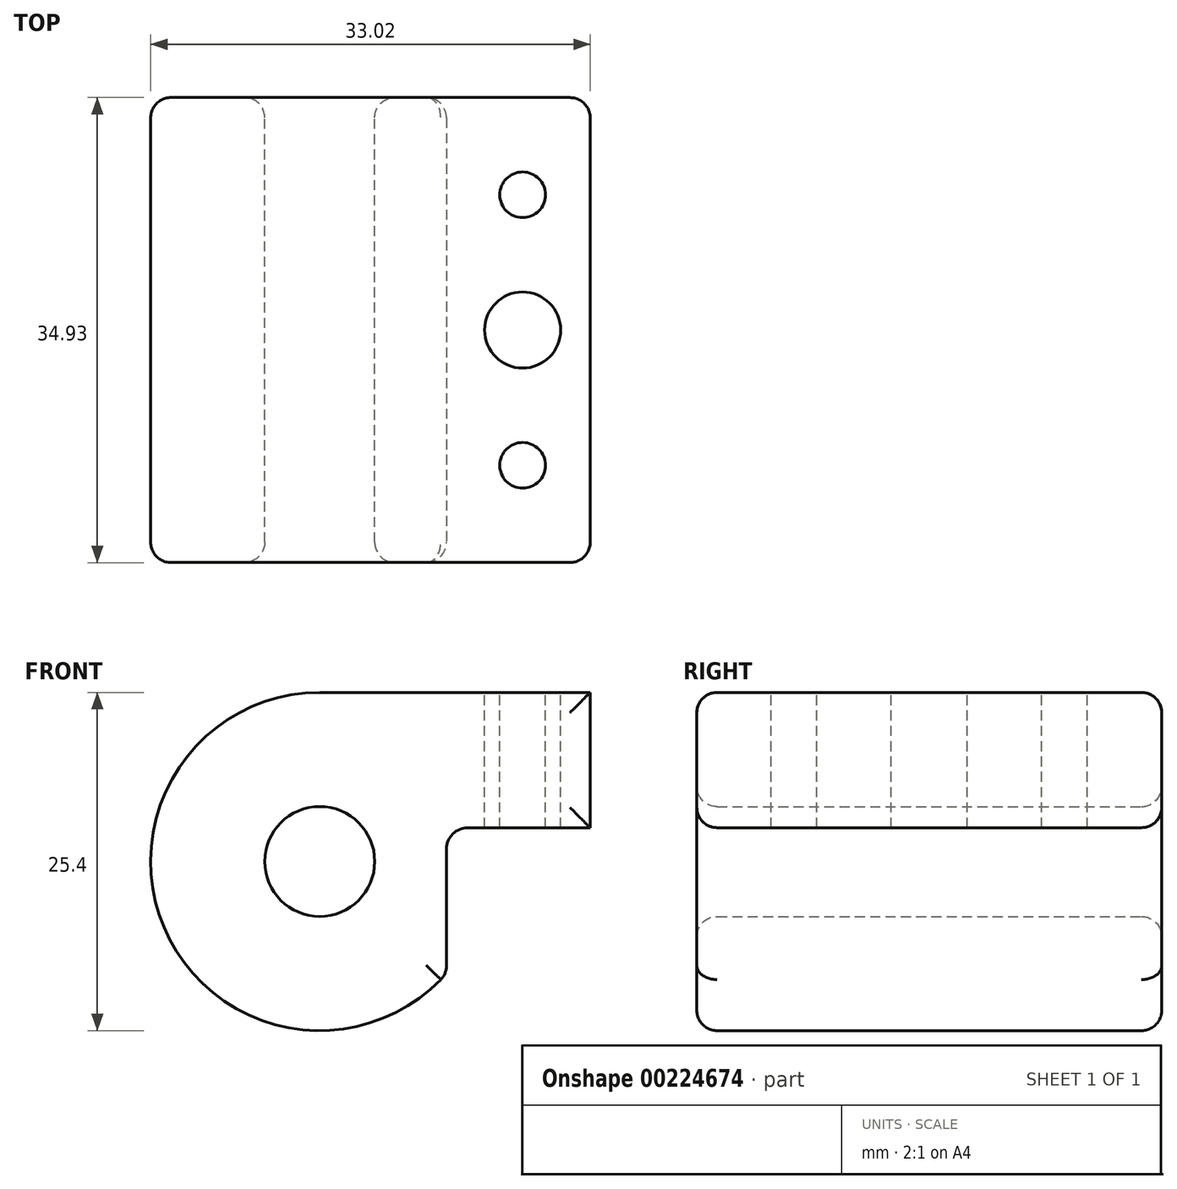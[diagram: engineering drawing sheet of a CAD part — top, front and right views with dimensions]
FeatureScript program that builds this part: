
annotation { "Feature Type Name" : "Feature", "Feature Type Description" : "" }
export const myFeature = defineFeature(function(context is Context, id is Id, definition is map)
    precondition{}
    {
        {
            var Q0;
            Q0=qCreatedBy(makeId("Front.planeOp"),FACE);
            var sketch = newSketch(context, id + "F0", { "sketchPlane" : qUnion([Q0])});
            skCircle(sketch, "E0", {"center": v(0, 0) * mm, "radius": 4.13 * mm});
            skArc(sketch, "E1", {"start": v(0, 12.7) * mm, "mid": v(-11.58, -5.23) * mm, "end": v(9.52, -8.4) * mm});
            skLineSegment(sketch, "E2", {"start": v(0, 12.7) * mm, "end": v(20.32, 12.7) * mm});
            skLineSegment(sketch, "E3", {"start": v(20.32, 12.7) * mm, "end": v(20.32, 2.54) * mm});
            skLineSegment(sketch, "E4", {"start": v(20.32, 2.54) * mm, "end": v(12.44, 2.54) * mm});
            skLineSegment(sketch, "E5", {"start": v(12.44, 2.54) * mm, "end": v(9.53, 2.54) * mm});
            skLineSegment(sketch, "E6", {"start": v(9.53, 2.54) * mm, "end": v(9.53, -8.4) * mm});
            skSolve(sketch);
        }
        {
            var Q0;
            Q0=makeQuery(id+"F0.imprint","IMPRINT",FACE,{"disambiguationData":[TD([[makeQuery(id+"F0.imprint","IMPRINT",EDGE,{"derivedFrom":sQuery(id+"F0.wireOp",EDGE,"E0")}),-1.0]])]});
            extrude(context, id + "F1", {"entities" : qUnion([Q0]), "depth" : 34.92 * mm});
        }
        {
            var Q0;
            Q0=makeQuery(id+"F1.opExtrude","SWEPT_FACE",FACE,{"disambiguationData":[OSD([sQuery(id+"F0.wireOp",EDGE,"E2")])]});
            var sketch = newSketch(context, id + "F2", { "sketchPlane" : qUnion([Q0])});
            skLineSegment(sketch, "E7", {"start": v(15.24, 0) * mm, "end": v(15.24, -34.93) * mm, "construction": true});
            skCircle(sketch, "E8", {"center": v(15.24, -17.46) * mm, "radius": 2.86 * mm});
            skCircle(sketch, "E9", {"center": v(15.24, -27.62) * mm, "radius": 1.71 * mm});
            skCircle(sketch, "E10", {"center": v(15.24, -7.3) * mm, "radius": 1.71 * mm});
            skSolve(sketch);
        }
        {
            var Q0;
            Q0 = qSketchRegion(id + "F2", true);
            extrude(context, id + "F3", {"entities" : qUnion([Q0]), "operationType" : NewBodyOperationType.REMOVE, "oppositeDirection" : true, "depth" : 25.4 * mm});
        }
        {
            var Q0;
            Q0=makeQuery(id+"F1.opExtrude","SWEPT_EDGE",EDGE,{"disambiguationData":[OSD([sQuery(id+"F0.wireOp",EDGE,"E5"),sQuery(id+"F0.wireOp",EDGE,"E6")])]});
            fillet(context, id + "F4", {"entities" : qUnion([Q0]), "radius" : 1.6 * mm, "tangentPropagation" : true, "allowEdgeOverflow" : false});
        }
        {
            var Q0;
            Q0=makeQuery(id+"F1.opExtrude","CAP_FACE",FACE,{"disambiguationData":[OSD([sQuery(id+"F0.wireOp",EDGE,"E0"),sQuery(id+"F0.wireOp",EDGE,"E1"),sQuery(id+"F0.wireOp",EDGE,"E2"),sQuery(id+"F0.wireOp",EDGE,"E3"),sQuery(id+"F0.wireOp",EDGE,"E4"),sQuery(id+"F0.wireOp",EDGE,"E5"),sQuery(id+"F0.wireOp",EDGE,"E6")])],"isStart":false});
            fillet(context, id + "F5", {"entities" : qUnion([Q0]), "radius" : 1.52 * mm, "tangentPropagation" : true, "allowEdgeOverflow" : false});
        }
        {
            var Q0;
            Q0=makeQuery(id+"F1.opExtrude","CAP_FACE",FACE,{"disambiguationData":[OSD([sQuery(id+"F0.wireOp",EDGE,"E0"),sQuery(id+"F0.wireOp",EDGE,"E1"),sQuery(id+"F0.wireOp",EDGE,"E2"),sQuery(id+"F0.wireOp",EDGE,"E3"),sQuery(id+"F0.wireOp",EDGE,"E4"),sQuery(id+"F0.wireOp",EDGE,"E5"),sQuery(id+"F0.wireOp",EDGE,"E6")])],"isStart":true});
            fillet(context, id + "F6", {"entities" : qUnion([Q0]), "radius" : 1.52 * mm, "tangentPropagation" : true, "allowEdgeOverflow" : false});
        }
        {
            var Q0;
            Q0=makeQuery(id+"F1.opExtrude","SWEPT_EDGE",EDGE,{"disambiguationData":[OSD([sQuery(id+"F0.wireOp",EDGE,"E1"),sQuery(id+"F0.wireOp",EDGE,"E6")])]});
            fillet(context, id + "F7", {"entities" : qUnion([Q0]), "radius" : 1.52 * mm, "tangentPropagation" : true, "allowEdgeOverflow" : false});
        }
    });
